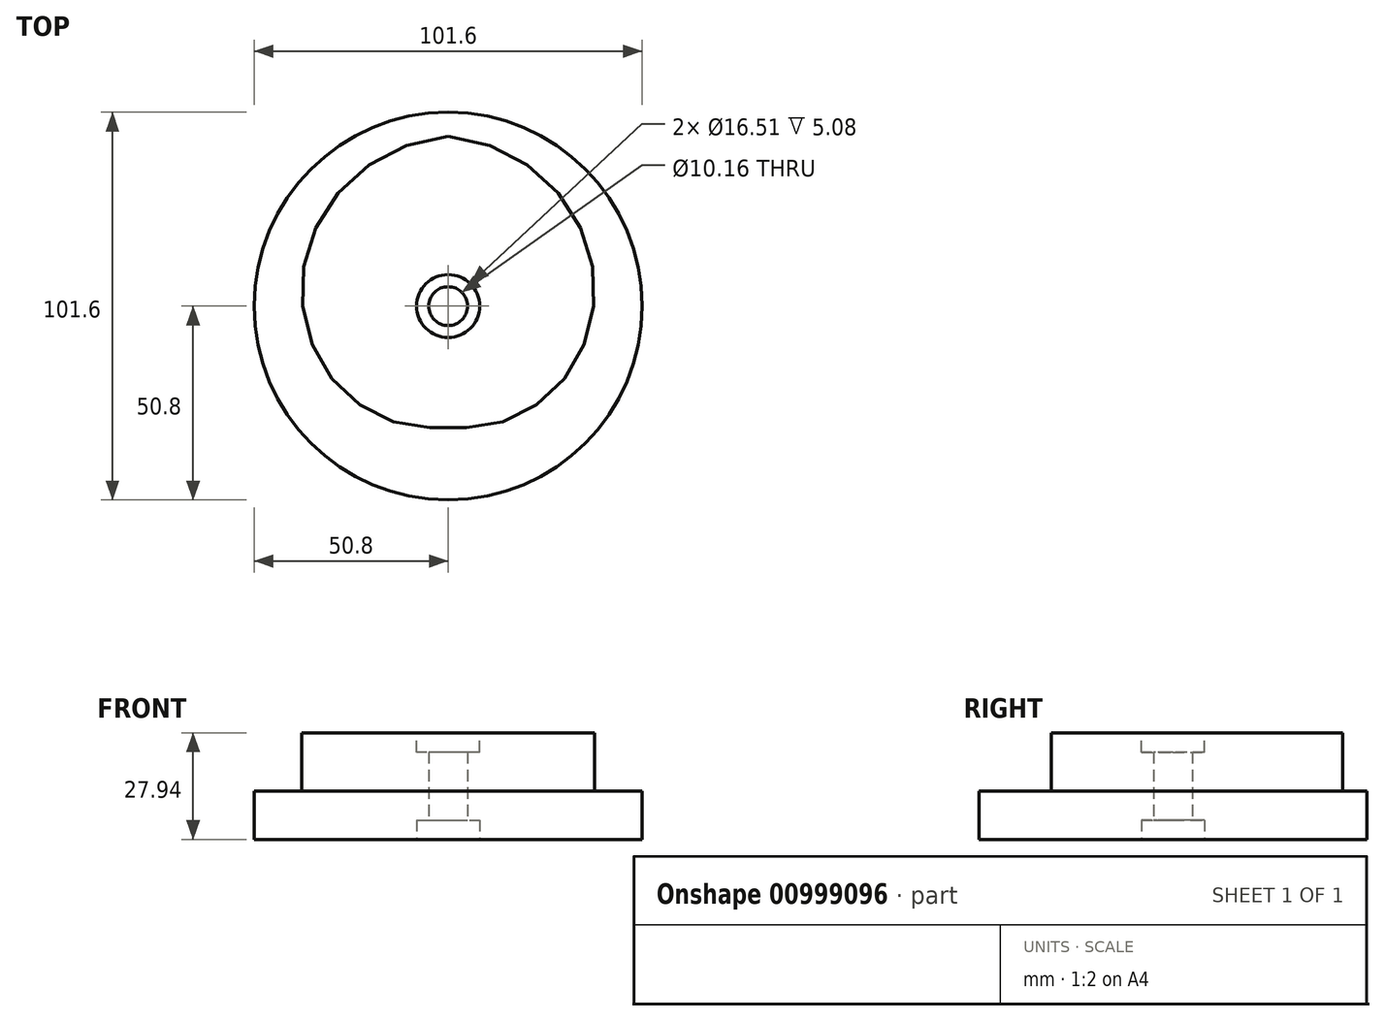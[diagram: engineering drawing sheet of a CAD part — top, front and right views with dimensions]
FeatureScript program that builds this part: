
annotation { "Feature Type Name" : "Feature", "Feature Type Description" : "" }
export const myFeature = defineFeature(function(context is Context, id is Id, definition is map)
    precondition{}
    {
        {
            var Q0;
            Q0=qCreatedBy(makeId("Top.planeOp"),FACE);
            var sketch = newSketch(context, id + "F0", { "sketchPlane" : qUnion([Q0])});
            skCircle(sketch, "E0", {"center": v(0, 0) * mm, "radius": 44.45 * mm});
            skSolve(sketch);
        }
        {
            var Q0;
            Q0 = qSketchRegion(id + "F0", true);
            extrude(context, id + "F1", {"entities" : qUnion([Q0]), "depth" : 12.7 * mm, "offsetDistance" : 25.4 * mm});
        }
        {
            var Q0;
            Q0=makeQuery(id+"F1.opExtrude","CAP_FACE",FACE,{"disambiguationData":[OSD([sQuery(id+"F0.wireOp",EDGE,"E0")])],"isStart":false});
            var sketch = newSketch(context, id + "F2", { "sketchPlane" : qUnion([Q0])});
            skLineSegment(sketch, "E1", {"start": v(0, 0) * mm, "end": v(0, 44.45) * mm});
            skSolve(sketch);
        }
        {
            var Q0;
            Q0=makeQuery(id+"F2.imprint","IMPRINT",FACE,{"disambiguationData":[TD([[makeQuery(id+"F2.imprint","IMPRINT",EDGE,{"derivedFrom":makeQuery(id+"F1.opExtrude","CAP_EDGE",EDGE,{"disambiguationData":[OSD([sQuery(id+"F0.wireOp",EDGE,"E0")])],"isStart":false})}),1.0]])]});
            var sketch = newSketch(context, id + "F3", { "sketchPlane" : qUnion([Q0])});
            skLineSegment(sketch, "E2", {"start": v(0, -44.45) * mm, "end": v(0, -31.75) * mm});
            skLineSegment(sketch, "E3", {"start": v(8.5, -31.7) * mm, "end": v(11.5, -42.94) * mm});
            skLineSegment(sketch, "E4", {"start": v(16.93, -29.33) * mm, "end": v(22.22, -38.5) * mm});
            skLineSegment(sketch, "E5", {"start": v(24.7, -24.7) * mm, "end": v(31.43, -31.43) * mm});
            skLineSegment(sketch, "E6", {"start": v(31.16, -18) * mm, "end": v(38.5, -22.23) * mm});
            skLineSegment(sketch, "E7", {"start": v(35.78, -9.59) * mm, "end": v(42.94, -11.5) * mm});
            skLineSegment(sketch, "E8", {"start": v(38.1, 0) * mm, "end": v(44.45, 0) * mm});
            skLineSegment(sketch, "E9", {"start": v(37.82, 10.13) * mm, "end": v(42.94, 11.5) * mm});
            skLineSegment(sketch, "E10", {"start": v(34.83, 20.1) * mm, "end": v(38.5, 22.22) * mm});
            skLineSegment(sketch, "E11", {"start": v(29.19, 29.19) * mm, "end": v(31.43, 31.43) * mm});
            skLineSegment(sketch, "E12", {"start": v(21.17, 36.66) * mm, "end": v(22.23, 38.5) * mm});
            skLineSegment(sketch, "E13", {"start": v(11.23, 41.91) * mm, "end": v(11.5, 42.94) * mm});
            skLineSegment(sketch, "E14.MirrorCS", {"start": v(-8.5, -31.7) * mm, "end": v(-11.5, -42.94) * mm});
            skLineSegment(sketch, "E15.MirrorCS", {"start": v(-16.93, -29.33) * mm, "end": v(-22.22, -38.5) * mm});
            skLineSegment(sketch, "E16.MirrorCS", {"start": v(-24.7, -24.7) * mm, "end": v(-31.43, -31.43) * mm});
            skLineSegment(sketch, "E17.MirrorCS", {"start": v(-31.16, -18) * mm, "end": v(-38.5, -22.23) * mm});
            skLineSegment(sketch, "E18.MirrorCS", {"start": v(-35.78, -9.59) * mm, "end": v(-42.94, -11.5) * mm});
            skLineSegment(sketch, "E19.MirrorCS", {"start": v(-38.1, 0) * mm, "end": v(-44.45, 0) * mm});
            skLineSegment(sketch, "E20.MirrorCS", {"start": v(-37.82, 10.13) * mm, "end": v(-42.94, 11.5) * mm});
            skLineSegment(sketch, "E21.MirrorCS", {"start": v(-34.83, 20.1) * mm, "end": v(-38.5, 22.22) * mm});
            skLineSegment(sketch, "E22.MirrorCS", {"start": v(-29.19, 29.19) * mm, "end": v(-31.43, 31.43) * mm});
            skLineSegment(sketch, "E23.MirrorCS", {"start": v(-21.17, 36.66) * mm, "end": v(-22.23, 38.5) * mm});
            skLineSegment(sketch, "E24.MirrorCS", {"start": v(-11.23, 41.91) * mm, "end": v(-11.5, 42.94) * mm});
            skSolve(sketch);
        }
        {
            var Q0;
            {var subQ0=makeQuery(id+"F2.imprint","IMPRINT",EDGE,{"derivedFrom":makeQuery(id+"F1.opExtrude","CAP_EDGE",EDGE,{"disambiguationData":[OSD([sQuery(id+"F0.wireOp",EDGE,"E0")])],"isStart":false})});var subQ17=makeQuery(id+"F3.imprint","IMPRINT",VERTEX,{"disambiguationData":[OD(0.0)],"derivedFrom":subQ0});Q0=makeQuery(id+"F3.imprint","IMPRINT",FACE,{"disambiguationData":[TD([[makeQuery(id+"F3.imprint","IMPRINT",EDGE,{"disambiguationData":[TD([[subQ17,1.0]])],"derivedFrom":subQ0}),1.0]])]});}
            var sketch = newSketch(context, id + "F4", { "sketchPlane" : qUnion([Q0])});
            skFitSpline(sketch, "E25", {"points": [v(0, 44.45) * mm, v(11.23, 41.91) * mm, v(21.17, 36.66) * mm, v(29.19, 29.19) * mm, v(34.83, 20.1) * mm, v(37.82, 10.13) * mm, v(38.1, 0) * mm, v(35.78, -9.59) * mm, v(31.16, -18) * mm, v(24.7, -24.7) * mm, v(16.93, -29.33) * mm, v(8.5, -31.7) * mm, v(0, -31.75) * mm, v(-8.5, -31.7) * mm, v(-16.93, -29.33) * mm, v(-24.7, -24.7) * mm, v(-31.16, -18) * mm, v(-35.78, -9.59) * mm, v(-38.1, 0) * mm, v(-37.82, 10.13) * mm, v(-34.83, 20.1) * mm, v(-29.19, 29.19) * mm, v(-21.17, 36.66) * mm, v(-11.23, 41.91) * mm, v(0, 44.45) * mm]});
            skSolve(sketch);
        }
        {
            var Q0;
            Q0 = qSketchRegion(id + "F4", true);
            extrude(context, id + "F5", {"entities" : qUnion([Q0]), "operationType" : NewBodyOperationType.ADD, "depth" : 15.24 * mm, "offsetDistance" : 25.4 * mm});
        }
        {
            var Q0;
            Q0=makeQuery(id+"F1.opExtrude","CAP_FACE",FACE,{"disambiguationData":[OSD([sQuery(id+"F0.wireOp",EDGE,"E0")])],"isStart":true});
            var sketch = newSketch(context, id + "F6", { "sketchPlane" : qUnion([Q0])});
            skCircle(sketch, "E26", {"center": v(0, 0) * mm, "radius": 5.08 * mm});
            skSolve(sketch);
        }
        {
            var Q0;
            Q0 = qSketchRegion(id + "F6", true);
            extrude(context, id + "F7", {"entities" : qUnion([Q0]), "operationType" : NewBodyOperationType.REMOVE, "endBound" : BoundingType.THROUGH_ALL, "oppositeDirection" : true, "depth" : 25.4 * mm, "offsetDistance" : 25.4 * mm});
        }
        {
            var Q0;
            Q0=makeQuery(id+"F1.opExtrude","CAP_FACE",FACE,{"disambiguationData":[OSD([sQuery(id+"F0.wireOp",EDGE,"E0")])],"isStart":true});
            var sketch = newSketch(context, id + "F8", { "sketchPlane" : qUnion([Q0])});
            skCircle(sketch, "E27", {"center": v(0, 0) * mm, "radius": 44.45 * mm});
            skCircle(sketch, "E28", {"center": v(0, 0) * mm, "radius": 50.8 * mm});
            skSolve(sketch);
        }
        {
            var Q0;
            Q0 = qSketchRegion(id + "F8", true);
            var Q1;
            Q1=makeQuery(id+"F1.opExtrude","CAP_FACE",FACE,{"disambiguationData":[OSD([sQuery(id+"F0.wireOp",EDGE,"E0")])],"isStart":false});
            extrude(context, id + "F9", {"entities" : qUnion([Q0]), "operationType" : NewBodyOperationType.ADD, "endBound" : BoundingType.UP_TO_SURFACE, "oppositeDirection" : true, "depth" : 12.7 * mm, "endBoundEntityFace" : qUnion([Q1]), "offsetDistance" : 25.4 * mm});
        }
        {
            var Q0;
            Q0=makeQuery(id+"F9.boolean.opBoolean","MERGE",FACE,{"derivedFrom":[makeQuery(id+"F1.opExtrude","CAP_FACE",FACE,{"disambiguationData":[OSD([sQuery(id+"F0.wireOp",EDGE,"E0")])],"isStart":true}),makeQuery(id+"F9.opExtrude","CAP_FACE",FACE,{"disambiguationData":[OSD([sQuery(id+"F8.wireOp",EDGE,"E27"),sQuery(id+"F8.wireOp",EDGE,"E28")])],"isStart":true})]});
            var sketch = newSketch(context, id + "F10", { "sketchPlane" : qUnion([Q0])});
            skCircle(sketch, "E29", {"center": v(0, 0) * mm, "radius": 8.26 * mm});
            skSolve(sketch);
        }
        {
            var Q0;
            Q0 = qSketchRegion(id + "F10", true);
            extrude(context, id + "F11", {"entities" : qUnion([Q0]), "operationType" : NewBodyOperationType.REMOVE, "oppositeDirection" : true, "depth" : 5.08 * mm, "offsetDistance" : 25.4 * mm});
        }
        {
            var Q0;
            Q0=makeQuery(id+"F5.opExtrude","CAP_FACE",FACE,{"disambiguationData":[OSD([sQuery(id+"F4.wireOp",EDGE,"E25")])],"isStart":false});
            var sketch = newSketch(context, id + "F12", { "sketchPlane" : qUnion([Q0])});
            skCircle(sketch, "E30", {"center": v(0, 0) * mm, "radius": 8.26 * mm});
            skSolve(sketch);
        }
        {
            var Q0;
            Q0 = qSketchRegion(id + "F12", true);
            extrude(context, id + "F13", {"entities" : qUnion([Q0]), "operationType" : NewBodyOperationType.REMOVE, "oppositeDirection" : true, "depth" : 5.08 * mm, "offsetDistance" : 25.4 * mm});
        }
    });
